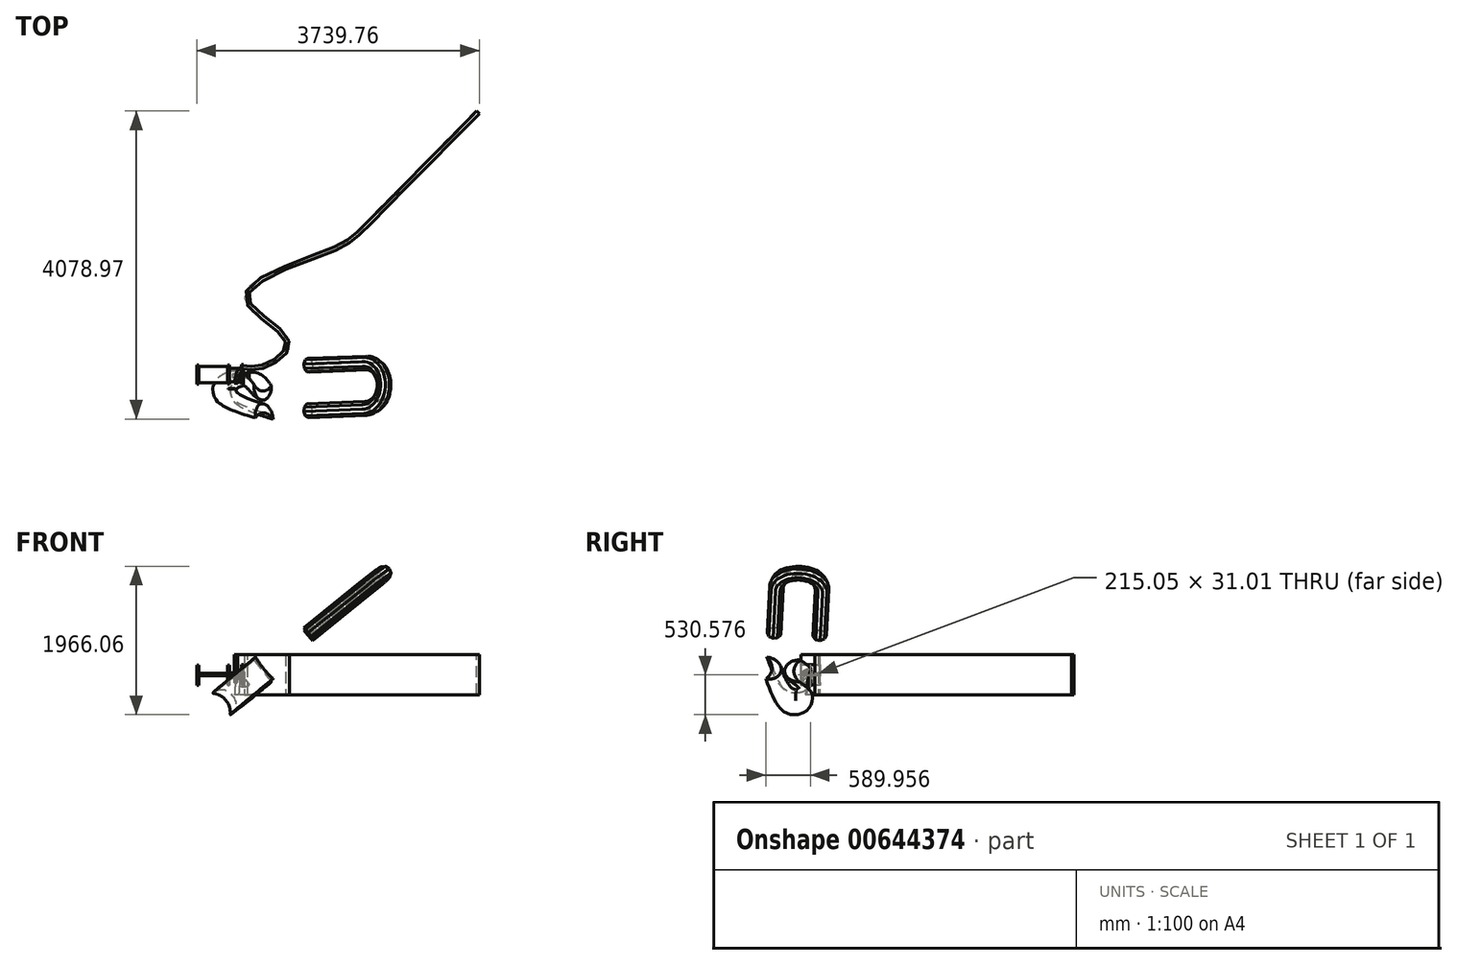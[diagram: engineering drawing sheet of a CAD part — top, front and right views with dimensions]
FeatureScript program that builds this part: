
annotation { "Feature Type Name" : "Feature", "Feature Type Description" : "" }
export const myFeature = defineFeature(function(context is Context, id is Id, definition is map)
    precondition{}
    {
        {
            var Q0;
            Q0=qCreatedBy(makeId("Front.planeOp"),FACE);
            var sketch = newSketch(context, id + "F0", { "sketchPlane" : qUnion([Q0])});
            skArc(sketch, "E0", {"start": v(0, 0) * mm, "mid": v(42.62, -98.33) * mm, "end": v(149.7, -102.29) * mm});
            skSolve(sketch);
        }
        {
            var Q0;
            Q0=qCreatedBy(makeId("Top.planeOp"),FACE);
            var sketch = newSketch(context, id + "F1", { "sketchPlane" : qUnion([Q0])});
            skLineSegment(sketch, "E1.bottom", {"start": v(44.25, -19.6) * mm, "end": v(-44.25, -19.6) * mm});
            skLineSegment(sketch, "E1.top", {"start": v(44.25, 19.6) * mm, "end": v(-44.25, 19.6) * mm});
            skLineSegment(sketch, "E1.left", {"start": v(44.25, -19.6) * mm, "end": v(44.25, 19.6) * mm});
            skLineSegment(sketch, "E1.right", {"start": v(-44.25, -19.6) * mm, "end": v(-44.25, 19.6) * mm});
            skPoint(sketch, "E1.middle", {"position": v(0, 0) * mm});
            skSolve(sketch);
        }
        {
            var Q0;
            Q0 = qSketchRegion(id + "F1", true);
            var Q1;
            Q1 = qBodyType(qCreatedBy(id + "F0" ,EDGE), BodyType.WIRE);
            sweep(context, id + "F2", {"profiles" : qUnion([Q0]), "path" : qUnion([Q1])});
        }
        {
            var Q0;
            Q0=makeQuery(id+"F2.opSweep","CAP_FACE",FACE,{"disambiguationData":[OSD([sQuery(id+"F0.wireOp",VERTEX,"E0.end"),sQuery(id+"F1.wireOp",EDGE,"E1.bottom"),sQuery(id+"F1.wireOp",EDGE,"E1.top"),sQuery(id+"F1.wireOp",EDGE,"E1.left"),sQuery(id+"F1.wireOp",EDGE,"E1.right")])],"isStart":false});
            cPlane(context, id + "F3", {"entities" : qUnion([Q0]), "cplaneType" : CPlaneType.OFFSET, "offset" : 254 * mm, "width" : 152.4 * mm, "height" : 152.4 * mm});
        }
        {
            var Q0;
            Q0=qCreatedBy(id+"F3.planeOp",FACE);
            var sketch = newSketch(context, id + "F4", { "sketchPlane" : qUnion([Q0])});
            skArc(sketch, "E2", {"start": v(-116.5, 0) * mm, "mid": v(-200.77, -180.77) * mm, "end": v(-130.9, -367.57) * mm});
            skArc(sketch, "E3", {"start": v(-116.5, 0) * mm, "mid": v(-322.75, -175.99) * mm, "end": v(-130.9, -367.57) * mm});
            skPoint(sketch, "E4", {"position": v(-263.54, -183.21) * mm});
            skSolve(sketch);
        }
        {
            var Q0;
            Q0=sQuery(id+"F4.wireOp",EDGE,"E2");
            var Q1;
            Q1=sQuery(id+"F4.wireOp",EDGE,"E3");
            cPlane(context, id + "F5", {"entities" : qUnion([Q0, Q1]), "cplaneType" : CPlaneType.LINE_ANGLE, "offset" : 25.4 * mm, "angle" : 0 * degree, "width" : 152.4 * mm, "height" : 152.4 * mm});
        }
        {
            var Q0;
            Q0=qCreatedBy(id+"F5.planeOp",FACE);
            var sketch = newSketch(context, id + "F6", { "sketchPlane" : qUnion([Q0])});
            skPoint(sketch, "E5.0", {"position": v(298.06, 265.7) * mm});
            skFitSpline(sketch, "E6", {"points": [v(311.69, 430.8) * mm, v(-260.2, 165.64) * mm, v(15.38, 74.69) * mm, v(298.06, 265.7) * mm], "startDerivative": vector(-2323.33, -611.56) * mm, "endDerivative": vector(1051.78, 461.93) * mm});
            skSolve(sketch);
        }
        {
            var Q0;
            Q0=makeQuery(id+"F4.imprint","IMPRINT",FACE,{"disambiguationData":[TD([[makeQuery(id+"F4.imprint","IMPRINT",EDGE,{"derivedFrom":sQuery(id+"F4.wireOp",EDGE,"E2")}),-1.0]])]});
            var Q1;
            Q1=sQuery(id+"F6.wireOp",EDGE,"E6");
            sweep(context, id + "F7", {"profiles" : qUnion([Q0]), "path" : qUnion([Q1])});
        }
        {
            var Q0;
            Q0=qCreatedBy(id+"F5.planeOp",FACE);
            var sketch = newSketch(context, id + "F8", { "sketchPlane" : qUnion([Q0])});
            skLineSegment(sketch, "E7", {"start": v(1077.23, -110.67) * mm, "end": v(2064.8, -110.67) * mm});
            skArc(sketch, "E8", {"start": v(2064.8, -110.67) * mm, "mid": v(2363.94, 188.47) * mm, "end": v(2064.8, 487.61) * mm});
            skLineSegment(sketch, "E9", {"start": v(2064.8, 487.61) * mm, "end": v(1077.23, 487.61) * mm});
            skSolve(sketch);
        }
        {
            var Q0;
            Q0=sQuery(id+"F8.wireOp",VERTEX,"E7.start");
            var Q1;
            Q1=sQuery(id+"F8.wireOp",EDGE,"E7");
            cPlane(context, id + "F9", {"entities" : qUnion([Q0, Q1]), "cplaneType" : CPlaneType.LINE_POINT, "offset" : 25.4 * mm, "width" : 152.4 * mm, "height" : 152.4 * mm});
        }
        {
            var Q0;
            Q0=qCreatedBy(id+"F9.planeOp",FACE);
            var sketch = newSketch(context, id + "F10", { "sketchPlane" : qUnion([Q0])});
            skPoint(sketch, "E10.0", {"position": v(103.2, -192.68) * mm});
            skCircle(sketch, "E11.cCircle", {"center": v(103.2, -192.68) * mm, "radius": 92.24 * mm, "construction": true});
            skLineSegment(sketch, "E11.0", {"start": v(14.79, -218.96) * mm, "end": v(18.58, -155.98) * mm});
            skLineSegment(sketch, "E11.1", {"start": v(18.58, -155.98) * mm, "end": v(61.96, -110.17) * mm});
            skLineSegment(sketch, "E11.2", {"start": v(61.96, -110.17) * mm, "end": v(124.64, -102.97) * mm});
            skLineSegment(sketch, "E11.3", {"start": v(124.64, -102.97) * mm, "end": v(177.3, -137.74) * mm});
            skLineSegment(sketch, "E11.4", {"start": v(177.3, -137.74) * mm, "end": v(195.27, -198.22) * mm});
            skLineSegment(sketch, "E11.5", {"start": v(195.27, -198.22) * mm, "end": v(170.17, -256.1) * mm});
            skLineSegment(sketch, "E11.6", {"start": v(170.17, -256.1) * mm, "end": v(113.73, -284.3) * mm});
            skLineSegment(sketch, "E11.7", {"start": v(113.73, -284.3) * mm, "end": v(52.37, -269.64) * mm});
            skLineSegment(sketch, "E11.8", {"start": v(52.37, -269.64) * mm, "end": v(14.79, -218.96) * mm});
            skSolve(sketch);
        }
        {
            var Q0;
            Q0=makeQuery(id+"F10.imprint","IMPRINT",FACE,{"disambiguationData":[TD([[makeQuery(id+"F10.imprint","IMPRINT",EDGE,{"derivedFrom":sQuery(id+"F10.wireOp",EDGE,"E11.0")}),-1.0]])]});
            var Q1;
            Q1=sQuery(id+"F8.wireOp",EDGE,"E7");
            var Q2;
            Q2=sQuery(id+"F8.wireOp",EDGE,"E8");
            var Q3;
            Q3=sQuery(id+"F8.wireOp",EDGE,"E9");
            sweep(context, id + "F11", {"profiles" : qUnion([Q0]), "path" : qUnion([Q1, Q2, Q3])});
        }
        {
            var Q0;
            Q0=qCreatedBy(makeId("Top.planeOp"),FACE);
            var sketch = newSketch(context, id + "F12", { "sketchPlane" : qUnion([Q0])});
            skFitSpline(sketch, "E12", {"points": [v(0, -101.53) * mm, v(74.08, 106.17) * mm, v(217.21, 100.77) * mm, v(597.7, 257.03) * mm, v(644.14, 525.84) * mm, v(135.42, 1054.91) * mm, v(1283.83, 1675.66) * mm, v(1700.65, 1965.4) * mm, v(3203.05, 3489.6) * mm], "startDerivative": vector(688.83, 3623.5) * mm, "endDerivative": vector(7747.14, 7863.33) * mm});
            skSolve(sketch);
        }
        {
            var Q0;
            Q0=sQuery(id+"F12.wireOp",VERTEX,"E12.end");
            var Q1;
            Q1=sQuery(id+"F12.wireOp",EDGE,"E12");
            cPlane(context, id + "F13", {"entities" : qUnion([Q0, Q1]), "cplaneType" : CPlaneType.CURVE_POINT, "offset" : 25.4 * mm, "width" : 152.4 * mm, "height" : 152.4 * mm});
        }
        {
            var Q0;
            Q0=qCreatedBy(id+"F13.planeOp",FACE);
            var sketch = newSketch(context, id + "F14", { "sketchPlane" : qUnion([Q0])});
            skPoint(sketch, "E13.0", {"position": v(167.4, 0) * mm});
            skLineSegment(sketch, "E14.bottom", {"start": v(143.99, -265.33) * mm, "end": v(190.8, -265.33) * mm});
            skLineSegment(sketch, "E14.top", {"start": v(143.99, 265.33) * mm, "end": v(190.8, 265.33) * mm});
            skLineSegment(sketch, "E14.left", {"start": v(143.99, -265.33) * mm, "end": v(143.99, 265.33) * mm});
            skLineSegment(sketch, "E14.right", {"start": v(190.8, -265.33) * mm, "end": v(190.8, 265.33) * mm});
            skSolve(sketch);
        }
        {
            var Q0;
            Q0=makeQuery(id+"F14.imprint","IMPRINT",FACE,{"disambiguationData":[TD([[makeQuery(id+"F14.imprint","IMPRINT",EDGE,{"derivedFrom":sQuery(id+"F14.wireOp",EDGE,"E14.bottom")}),1.0]])]});
            var Q1;
            Q1 = qBodyType(qCreatedBy(id + "F12" ,EDGE), BodyType.WIRE);
            sweep(context, id + "F15", {"profiles" : qUnion([Q0]), "path" : qUnion([Q1])});
        }
        {
            var Q0;
            Q0=qCreatedBy(makeId("Top.planeOp"),FACE);
            var sketch = newSketch(context, id + "F16", { "sketchPlane" : qUnion([Q0])});
            skLineSegment(sketch, "E15.bottom", {"start": v(-87.86, -77.95) * mm, "end": v(99.46, -77.95) * mm});
            skLineSegment(sketch, "E15.top", {"start": v(-87.86, 96.73) * mm, "end": v(99.46, 96.73) * mm});
            skLineSegment(sketch, "E15.left", {"start": v(-87.86, -77.95) * mm, "end": v(-87.86, 96.73) * mm});
            skLineSegment(sketch, "E15.right", {"start": v(99.46, -77.95) * mm, "end": v(99.46, 96.73) * mm});
            skSolve(sketch);
        }
        {
            var Q0;
            Q0=sQuery(id+"F16.wireOp",EDGE,"E15.right");
            var Q1;
            Q1=sQuery(id+"F16.wireOp",EDGE,"E15.top");
            cPlane(context, id + "F17", {"entities" : qUnion([Q0, Q1]), "cplaneType" : CPlaneType.LINE_ANGLE, "offset" : 25.4 * mm, "angle" : 90 * degree, "width" : 152.4 * mm, "height" : 152.4 * mm});
        }
        {
            var Q0;
            Q0=qCreatedBy(id+"F17.planeOp",FACE);
            var sketch = newSketch(context, id + "F18", { "sketchPlane" : qUnion([Q0])});
            skLineSegment(sketch, "E16.bottom", {"start": v(108.11, 129.96) * mm, "end": v(-146.59, 129.96) * mm});
            skLineSegment(sketch, "E16.top", {"start": v(108.11, -137.25) * mm, "end": v(-146.59, -137.25) * mm});
            skLineSegment(sketch, "E16.left", {"start": v(108.11, 129.96) * mm, "end": v(108.11, -137.25) * mm});
            skLineSegment(sketch, "E16.right", {"start": v(-146.59, 129.96) * mm, "end": v(-146.59, -137.25) * mm});
            skSolve(sketch);
        }
        {
            var Q0;
            Q0=makeQuery(id+"F18.imprint","IMPRINT",FACE,{"disambiguationData":[TD([[makeQuery(id+"F18.imprint","IMPRINT",EDGE,{"derivedFrom":sQuery(id+"F18.wireOp",EDGE,"E16.bottom")}),1.0]])]});
            extrude(context, id + "F19", {"entities" : qUnion([Q0]), "depth" : 25.4 * mm, "offsetDistance" : 25.4 * mm});
        }
        {
            var Q0;
            Q0=makeQuery(id+"F16.imprint","IMPRINT",FACE,{"disambiguationData":[TD([[makeQuery(id+"F16.imprint","IMPRINT",EDGE,{"derivedFrom":sQuery(id+"F16.wireOp",EDGE,"E15.bottom")}),1.0]])]});
            extrude(context, id + "F20", {"entities" : qUnion([Q0]), "operationType" : NewBodyOperationType.ADD, "depth" : 25.4 * mm, "offsetDistance" : 25.4 * mm});
        }
        {
            var Q0;
            Q0=makeQuery(id+"F20.opExtrude","CAP_EDGE",EDGE,{"disambiguationData":[OSD([sQuery(id+"F16.wireOp",EDGE,"E15.left")])],"isStart":true});
            var Q1;
            Q1=makeQuery(id+"F20.opExtrude","CAP_EDGE",EDGE,{"disambiguationData":[OSD([sQuery(id+"F16.wireOp",EDGE,"E15.top")])],"isStart":true});
            cPlane(context, id + "F21", {"entities" : qUnion([Q0, Q1]), "cplaneType" : CPlaneType.LINE_ANGLE, "offset" : 25.4 * mm, "angle" : 90 * degree, "width" : 152.4 * mm, "height" : 152.4 * mm});
        }
        {
            var Q0;
            Q0=qCreatedBy(id+"F21.planeOp",FACE);
            var sketch = newSketch(context, id + "F22", { "sketchPlane" : qUnion([Q0])});
            skLineSegment(sketch, "E17.bottom", {"start": v(-145.57, 127.63) * mm, "end": v(108.9, 127.63) * mm});
            skLineSegment(sketch, "E17.top", {"start": v(-145.57, -138.15) * mm, "end": v(108.9, -138.15) * mm});
            skLineSegment(sketch, "E17.left", {"start": v(-145.57, 127.63) * mm, "end": v(-145.57, -138.15) * mm});
            skLineSegment(sketch, "E17.right", {"start": v(108.9, 127.63) * mm, "end": v(108.9, -138.15) * mm});
            skSolve(sketch);
        }
        {
            var Q0;
            Q0 = qSketchRegion(id + "F22", true);
            extrude(context, id + "F23", {"entities" : qUnion([Q0]), "operationType" : NewBodyOperationType.ADD, "depth" : 25.4 * mm, "offsetDistance" : 25.4 * mm});
        }
        {
            var Q0;
            Q0=makeQuery(id+"F23.opExtrude","CAP_FACE",FACE,{"disambiguationData":[OSD([sQuery(id+"F22.wireOp",EDGE,"E17.bottom"),sQuery(id+"F22.wireOp",EDGE,"E17.top"),sQuery(id+"F22.wireOp",EDGE,"E17.left"),sQuery(id+"F22.wireOp",EDGE,"E17.right")])],"isStart":false});
            var sketch = newSketch(context, id + "F24", { "sketchPlane" : qUnion([Q0])});
            skLineSegment(sketch, "E18.bottom", {"start": v(-124.53, 14.94) * mm, "end": v(90.52, 14.94) * mm});
            skLineSegment(sketch, "E18.top", {"start": v(-124.53, -16.07) * mm, "end": v(90.52, -16.07) * mm});
            skLineSegment(sketch, "E18.left", {"start": v(-124.53, 14.94) * mm, "end": v(-124.53, -16.07) * mm});
            skLineSegment(sketch, "E18.right", {"start": v(90.52, 14.94) * mm, "end": v(90.52, -16.07) * mm});
            skSolve(sketch);
        }
        {
            var Q0;
            Q0 = qSketchRegion(id + "F24", true);
            extrude(context, id + "F25", {"entities" : qUnion([Q0]), "operationType" : NewBodyOperationType.ADD, "depth" : 381.38 * mm, "offsetDistance" : 25.4 * mm});
        }
        {
            var Q0;
            Q0=makeQuery(id+"F25.opExtrude","CAP_FACE",FACE,{"disambiguationData":[OSD([sQuery(id+"F24.wireOp",EDGE,"E18.bottom"),sQuery(id+"F24.wireOp",EDGE,"E18.top"),sQuery(id+"F24.wireOp",EDGE,"E18.left"),sQuery(id+"F24.wireOp",EDGE,"E18.right")])],"isStart":false});
            var sketch = newSketch(context, id + "F26", { "sketchPlane" : qUnion([Q0])});
            skLineSegment(sketch, "E19.bottom", {"start": v(-140.14, 127.35) * mm, "end": v(114.15, 127.35) * mm});
            skLineSegment(sketch, "E19.top", {"start": v(-140.14, -141.02) * mm, "end": v(114.15, -141.02) * mm});
            skLineSegment(sketch, "E19.left", {"start": v(-140.14, 127.35) * mm, "end": v(-140.14, -141.02) * mm});
            skLineSegment(sketch, "E19.right", {"start": v(114.15, 127.35) * mm, "end": v(114.15, -141.02) * mm});
            skSolve(sketch);
        }
        {
            var Q0;
            Q0 = qSketchRegion(id + "F26", true);
            extrude(context, id + "F27", {"entities" : qUnion([Q0]), "operationType" : NewBodyOperationType.ADD, "depth" : 25.4 * mm, "offsetDistance" : 25.4 * mm});
        }
    });
